# Revit family: L-Angle-Column
name_source: partatom
category: Structural Columns
revit_build: Autodesk Revit Architecture 2012 (Build: 20110210_1515)
units: mm (PartAtom-declared; Revit-internal decimal feet)

## types (127) — shared parameters
Assembly Code = B10

## per-type parameters (varying)
| type | A | W | b | d | k | t | x | y |
| L8X8X1-1/8 | 16.7 in² | 56.9 | 0' - 8" | 0' - 8" | 0' - 1 3/4" | 0' - 1 1/8" | 0' - 2 3/8" | 0' - 2 3/8" |
| L8X8X1 | 15 in² | 51 | 0' - 8" | 0' - 8" | 0' - 1 5/8" | 0' - 1" | 0' - 2 3/8" | 0' - 2 3/8" |
| L8X8X7/8 | 13.2 in² | 45 | 0' - 8" | 0' - 8" | 0' - 1 1/2" | 0' - 0 7/8" | 0' - 2 5/16" | 0' - 2 5/16" |
| L8X8X3/4 | 11.4 in² | 38.9 | 0' - 8" | 0' - 8" | 0' - 1 3/8" | 0' - 0 3/4" | 0' - 2 1/4" | 0' - 2 1/4" |
| L8X8X5/8 | 9.61 in² | 32.7 | 0' - 8" | 0' - 8" | 0' - 1 1/4" | 0' - 0 5/8" | 0' - 2 3/16" | 0' - 2 3/16" |
| L8X8X9/16 | 8.68 in² | 29.6 | 0' - 8" | 0' - 8" | 0' - 1 3/16" | 0' - 0 9/16" | 0' - 2 3/16" | 0' - 2 3/16" |
| L8X8X1/2 | 7.75 in² | 26.4 | 0' - 8" | 0' - 8" | 0' - 1 1/8" | 0' - 0 1/2" | 0' - 2 3/16" | 0' - 2 3/16" |
| L8X6X1 | 13 in² | 44.2 | 0' - 6" | 0' - 8" | 0' - 1 1/2" | 0' - 1" | 0' - 1 5/8" | 0' - 2 5/8" |
| L8X6X7/8 | 11.5 in² | 39.1 | 0' - 6" | 0' - 8" | 0' - 1 3/8" | 0' - 0 7/8" | 0' - 1 5/8" | 0' - 2 5/8" |
| L8X6X3/4 | 9.94 in² | 33.8 | 0' - 6" | 0' - 8" | 0' - 1 1/4" | 0' - 0 3/4" | 0' - 1 9/16" | 0' - 2 9/16" |
| L8X6X5/8 | 8.36 in² | 28.5 | 0' - 6" | 0' - 8" | 0' - 1 1/8" | 0' - 0 5/8" | 0' - 1 1/2" | 0' - 2 1/2" |
| L8X6X9/16 | 7.56 in² | 25.7 | 0' - 6" | 0' - 8" | 0' - 1 1/16" | 0' - 0 9/16" | 0' - 1 1/2" | 0' - 2 1/2" |
| L8X6X1/2 | 6.75 in² | 23 | 0' - 6" | 0' - 8" | 0' - 1" | 0' - 0 1/2" | 0' - 1 7/16" | 0' - 2 7/16" |
| L8X6X7/16 | 5.93 in² | 20.2 | 0' - 6" | 0' - 8" | 0' - 0 15/16" | 0' - 0 7/16" | 0' - 1 7/16" | 0' - 2 7/16" |
| L8X4X1 | 11 in² | 37.4 | 0' - 4" | 0' - 8" | 0' - 1 1/2" | 0' - 1" | 0' - 1 1/16" | 0' - 3" |
| L8X4X7/8 | 9.73 in² | 33.1 | 0' - 4" | 0' - 8" | 0' - 1 3/8" | 0' - 0 7/8" | 0' - 1" | 0' - 3" |
| L8X4X3/4 | 8.44 in² | 28.7 | 0' - 4" | 0' - 8" | 0' - 1 1/4" | 0' - 0 3/4" | 0' - 0 15/16" | 0' - 2 15/16" |
| L8X4X5/8 | 7.11 in² | 24.2 | 0' - 4" | 0' - 8" | 0' - 1 1/8" | 0' - 0 5/8" | 0' - 0 7/8" | 0' - 2 7/8" |
| L8X4X9/16 | 6.43 in² | 21.9 | 0' - 4" | 0' - 8" | 0' - 1 1/16" | 0' - 0 9/16" | 0' - 0 7/8" | 0' - 2 7/8" |
| L8X4X1/2 | 5.75 in² | 19.6 | 0' - 4" | 0' - 8" | 0' - 1" | 0' - 0 1/2" | 0' - 0 7/8" | 0' - 2 13/16" |
| L8X4X7/16 | 5.06 in² | 17.2 | 0' - 4" | 0' - 8" | 0' - 0 15/16" | 0' - 0 7/16" | 0' - 0 13/16" | 0' - 2 13/16" |
| L7X4X3/4 | 7.69 in² | 26.2 | 0' - 4" | 0' - 7" | 0' - 1 1/4" | 0' - 0 3/4" | 0' - 1" | 0' - 2 1/2" |
| L7X4X5/8 | 6.48 in² | 22.1 | 0' - 4" | 0' - 7" | 0' - 1 1/8" | 0' - 0 5/8" | 0' - 0 15/16" | 0' - 2 7/16" |
| L7X4X1/2 | 5.25 in² | 17.9 | 0' - 4" | 0' - 7" | 0' - 1" | 0' - 0 1/2" | 0' - 0 15/16" | 0' - 2 3/8" |
| L7X4X7/16 | 4.62 in² | 15.7 | 0' - 4" | 0' - 7" | 0' - 0 15/16" | 0' - 0 7/16" | 0' - 0 7/8" | 0' - 2 3/8" |
| L7X4X3/8 | 3.98 in² | 13.6 | 0' - 4" | 0' - 7" | 0' - 0 7/8" | 0' - 0 3/8" | 0' - 0 7/8" | 0' - 2 3/8" |
| L6X6X1 | 11 in² | 37.4 | 0' - 6" | 0' - 6" | 0' - 1 1/2" | 0' - 1" | 0' - 1 7/8" | 0' - 1 7/8" |
| L6X6X7/8 | 9.75 in² | 33.1 | 0' - 6" | 0' - 6" | 0' - 1 3/8" | 0' - 0 7/8" | 0' - 1 13/16" | 0' - 1 13/16" |
| L6X6X3/4 | 8.46 in² | 28.7 | 0' - 6" | 0' - 6" | 0' - 1 1/4" | 0' - 0 3/4" | 0' - 1 3/4" | 0' - 1 3/4" |
| L6X6X5/8 | 7.13 in² | 24.2 | 0' - 6" | 0' - 6" | 0' - 1 1/8" | 0' - 0 5/8" | 0' - 1 3/4" | 0' - 1 3/4" |
| L6X6X9/16 | 6.45 in² | 21.9 | 0' - 6" | 0' - 6" | 0' - 1 1/16" | 0' - 0 9/16" | 0' - 1 11/16" | 0' - 1 11/16" |
| L6X6X1/2 | 5.77 in² | 19.6 | 0' - 6" | 0' - 6" | 0' - 1" | 0' - 0 1/2" | 0' - 1 11/16" | 0' - 1 11/16" |
| L6X6X7/16 | 5.08 in² | 17.2 | 0' - 6" | 0' - 6" | 0' - 0 15/16" | 0' - 0 7/16" | 0' - 1 5/8" | 0' - 1 5/8" |
| L6X6X3/8 | 4.38 in² | 14.9 | 0' - 6" | 0' - 6" | 0' - 0 7/8" | 0' - 0 3/8" | 0' - 1 5/8" | 0' - 1 5/8" |
| L6X6X5/16 | 3.67 in² | 12.4 | 0' - 6" | 0' - 6" | 0' - 0 13/16" | 0' - 0 5/16" | 0' - 1 5/8" | 0' - 1 5/8" |
| L6X4X7/8 | 7.98 in² | 27.2 | 0' - 4" | 0' - 6" | 0' - 1 3/8" | 0' - 0 7/8" | 0' - 1 1/8" | 0' - 2 1/8" |
| L6X4X3/4 | 6.94 in² | 23.6 | 0' - 4" | 0' - 6" | 0' - 1 1/4" | 0' - 0 3/4" | 0' - 1 1/16" | 0' - 2 1/16" |
| L6X4X5/8 | 5.86 in² | 20 | 0' - 4" | 0' - 6" | 0' - 1 1/8" | 0' - 0 5/8" | 0' - 1" | 0' - 2" |
| L6X4X9/16 | 5.31 in² | 18.1 | 0' - 4" | 0' - 6" | 0' - 1 1/16" | 0' - 0 9/16" | 0' - 1" | 0' - 2" |
| L6X4X1/2 | 4.75 in² | 16.2 | 0' - 4" | 0' - 6" | 0' - 1" | 0' - 0 1/2" | 0' - 1" | 0' - 2" |
| L6X4X7/16 | 4.18 in² | 14.3 | 0' - 4" | 0' - 6" | 0' - 0 15/16" | 0' - 0 7/16" | 0' - 0 15/16" | 0' - 1 15/16" |
| L6X4X3/8 | 3.61 in² | 12.3 | 0' - 4" | 0' - 6" | 0' - 0 7/8" | 0' - 0 3/8" | 0' - 0 15/16" | 0' - 1 15/16" |
| L6X4X5/16 | 3.03 in² | 10.3 | 0' - 4" | 0' - 6" | 0' - 0 13/16" | 0' - 0 5/16" | 0' - 0 15/16" | 0' - 1 7/8" |
| L6X3-1/2X1/2 | 4.5 in² | 15.3 | 0' - 3 1/2" | 0' - 6" | 0' - 1" | 0' - 0 1/2" | 0' - 0 13/16" | 0' - 2 1/16" |
| L6X3-1/2X3/8 | 3.42 in² | 11.7 | 0' - 3 1/2" | 0' - 6" | 0' - 0 7/8" | 0' - 0 3/8" | 0' - 0 3/4" | 0' - 2" |
| L6X3-1/2X5/16 | 2.87 in² | 9.8 | 0' - 3 1/2" | 0' - 6" | 0' - 0 13/16" | 0' - 0 5/16" | 0' - 0 3/4" | 0' - 2" |
| L5X5X7/8 | 7.98 in² | 27.2 | 0' - 5" | 0' - 5" | 0' - 1 3/8" | 0' - 0 7/8" | 0' - 1 9/16" | 0' - 1 9/16" |
| L5X5X3/4 | 6.94 in² | 23.6 | 0' - 5" | 0' - 5" | 0' - 1 1/4" | 0' - 0 3/4" | 0' - 1 1/2" | 0' - 1 1/2" |
| L5X5X5/8 | 5.86 in² | 20 | 0' - 5" | 0' - 5" | 0' - 1 1/8" | 0' - 0 5/8" | 0' - 1 1/2" | 0' - 1 1/2" |
| L5X5X1/2 | 4.75 in² | 16.2 | 0' - 5" | 0' - 5" | 0' - 1" | 0' - 0 1/2" | 0' - 1 7/16" | 0' - 1 7/16" |
| L5X5X7/16 | 4.18 in² | 14.3 | 0' - 5" | 0' - 5" | 0' - 0 15/16" | 0' - 0 7/16" | 0' - 1 3/8" | 0' - 1 3/8" |
| L5X5X3/8 | 3.61 in² | 12.3 | 0' - 5" | 0' - 5" | 0' - 0 7/8" | 0' - 0 3/8" | 0' - 1 3/8" | 0' - 1 3/8" |
| L5X5X5/16 | 3.03 in² | 10.3 | 0' - 5" | 0' - 5" | 0' - 0 13/16" | 0' - 0 5/16" | 0' - 1 3/8" | 0' - 1 3/8" |
| L5X3-1/2X3/4 | 5.81 in² | 19.8 | 0' - 3 1/2" | 0' - 5" | 0' - 1 3/16" | 0' - 0 3/4" | 0' - 1" | 0' - 1 3/4" |
| L5X3-1/2X5/8 | 4.92 in² | 16.8 | 0' - 3 1/2" | 0' - 5" | 0' - 1 1/16" | 0' - 0 5/8" | 0' - 0 15/16" | 0' - 1 11/16" |
| L5X3-1/2X1/2 | 4 in² | 13.6 | 0' - 3 1/2" | 0' - 5" | 0' - 0 15/16" | 0' - 0 1/2" | 0' - 0 7/8" | 0' - 1 5/8" |
| L5X3-1/2X3/8 | 3.05 in² | 10.4 | 0' - 3 1/2" | 0' - 5" | 0' - 0 13/16" | 0' - 0 3/8" | 0' - 0 7/8" | 0' - 1 5/8" |
| L5X3-1/2X5/16 | 2.56 in² | 8.7 | 0' - 3 1/2" | 0' - 5" | 0' - 0 3/4" | 0' - 0 5/16" | 0' - 0 13/16" | 0' - 1 9/16" |
| L5X3-1/2X1/4 | 2.06 in² | 7 | 0' - 3 1/2" | 0' - 5" | 0' - 0 11/16" | 0' - 0 1/4" | 0' - 0 13/16" | 0' - 1 9/16" |
| L5X3X1/2 | 3.75 in² | 12.8 | 0' - 3" | 0' - 5" | 0' - 0 15/16" | 0' - 0 1/2" | 0' - 0 3/4" | 0' - 1 3/4" |
| L5X3X7/16 | 3.31 in² | 11.3 | 0' - 3" | 0' - 5" | 0' - 0 7/8" | 0' - 0 7/16" | 0' - 0 3/4" | 0' - 1 3/4" |
| L5X3X3/8 | 2.86 in² | 9.8 | 0' - 3" | 0' - 5" | 0' - 0 13/16" | 0' - 0 3/8" | 0' - 0 11/16" | 0' - 1 11/16" |
| L5X3X5/16 | 2.4 in² | 8.2 | 0' - 3" | 0' - 5" | 0' - 0 3/4" | 0' - 0 5/16" | 0' - 0 11/16" | 0' - 1 11/16" |
| L5X3X1/4 | 1.94 in² | 6.6 | 0' - 3" | 0' - 5" | 0' - 0 11/16" | 0' - 0 1/4" | 0' - 0 5/8" | 0' - 1 5/8" |
| L4X4X3/4 | 5.44 in² | 18.5 | 0' - 4" | 0' - 4" | 0' - 1 1/8" | 0' - 0 3/4" | 0' - 1 1/4" | 0' - 1 1/4" |
| L4X4X5/8 | 4.61 in² | 15.7 | 0' - 4" | 0' - 4" | 0' - 1" | 0' - 0 5/8" | 0' - 1 1/4" | 0' - 1 1/4" |
| L4X4X1/2 | 3.75 in² | 12.8 | 0' - 4" | 0' - 4" | 0' - 0 7/8" | 0' - 0 1/2" | 0' - 1 3/16" | 0' - 1 3/16" |
| L4X4X7/16 | 3.31 in² | 11.3 | 0' - 4" | 0' - 4" | 0' - 0 13/16" | 0' - 0 7/16" | 0' - 1 1/8" | 0' - 1 1/8" |
| L4X4X3/8 | 2.86 in² | 9.8 | 0' - 4" | 0' - 4" | 0' - 0 3/4" | 0' - 0 3/8" | 0' - 1 1/8" | 0' - 1 1/8" |
| L4X4X5/16 | 2.4 in² | 8.2 | 0' - 4" | 0' - 4" | 0' - 0 11/16" | 0' - 0 5/16" | 0' - 1 1/8" | 0' - 1 1/8" |
| L4X4X1/4 | 1.94 in² | 6.6 | 0' - 4" | 0' - 4" | 0' - 0 5/8" | 0' - 0 1/4" | 0' - 1 1/16" | 0' - 1 1/16" |
| L4X3-1/2X1/2 | 3.5 in² | 11.9 | 0' - 3 1/2" | 0' - 4" | 0' - 0 7/8" | 0' - 0 1/2" | 0' - 1" | 0' - 1 1/4" |
| L4X3-1/2X3/8 | 2.67 in² | 9.1 | 0' - 3 1/2" | 0' - 4" | 0' - 0 3/4" | 0' - 0 3/8" | 0' - 0 15/16" | 0' - 1 3/16" |
| L4X3-1/2X5/16 | 2.25 in² | 7.7 | 0' - 3 1/2" | 0' - 4" | 0' - 0 11/16" | 0' - 0 5/16" | 0' - 0 15/16" | 0' - 1 3/16" |
| L4X3-1/2X1/4 | 1.81 in² | 6.2 | 0' - 3 1/2" | 0' - 4" | 0' - 0 5/8" | 0' - 0 1/4" | 0' - 0 7/8" | 0' - 1 1/8" |
| L4X3X5/8 | 3.89 in² | 13.6 | 0' - 3" | 0' - 4" | 0' - 1" | 0' - 0 5/8" | 0' - 0 7/8" | 0' - 1 3/8" |
| L4X3X1/2 | 3.25 in² | 11.1 | 0' - 3" | 0' - 4" | 0' - 0 7/8" | 0' - 0 1/2" | 0' - 0 13/16" | 0' - 1 5/16" |
| L4X3X3/8 | 2.48 in² | 8.5 | 0' - 3" | 0' - 4" | 0' - 0 3/4" | 0' - 0 3/8" | 0' - 0 3/4" | 0' - 1 1/4" |
| L4X3X5/16 | 2.09 in² | 7.2 | 0' - 3" | 0' - 4" | 0' - 0 11/16" | 0' - 0 5/16" | 0' - 0 3/4" | 0' - 1 1/4" |
| L4X3X1/4 | 1.69 in² | 5.8 | 0' - 3" | 0' - 4" | 0' - 0 5/8" | 0' - 0 1/4" | 0' - 0 3/4" | 0' - 1 1/4" |
| L3-1/2X3-1/2X1/2 | 3.25 in² | 11.1 | 0' - 3 1/2" | 0' - 3 1/2" | 0' - 0 7/8" | 0' - 0 1/2" | 0' - 1 1/16" | 0' - 1 1/16" |
| L3-1/2X3-1/2X7/16 | 2.87 in² | 9.8 | 0' - 3 1/2" | 0' - 3 1/2" | 0' - 0 13/16" | 0' - 0 7/16" | 0' - 1" | 0' - 1" |
| L3-1/2X3-1/2X3/8 | 2.48 in² | 8.5 | 0' - 3 1/2" | 0' - 3 1/2" | 0' - 0 3/4" | 0' - 0 3/8" | 0' - 1" | 0' - 1" |
| L3-1/2X3-1/2X5/16 | 2.09 in² | 7.2 | 0' - 3 1/2" | 0' - 3 1/2" | 0' - 0 11/16" | 0' - 0 5/16" | 0' - 1" | 0' - 1" |
| L3-1/2X3-1/2X1/4 | 1.69 in² | 5.8 | 0' - 3 1/2" | 0' - 3 1/2" | 0' - 0 5/8" | 0' - 0 1/4" | 0' - 0 15/16" | 0' - 0 15/16" |
| L3-1/2X3X1/2 | 3 in² | 10.2 | 0' - 3" | 0' - 3 1/2" | 0' - 0 7/8" | 0' - 0 1/2" | 0' - 0 7/8" | 0' - 1 1/8" |
| L3-1/2X3X7/16 | 2.65 in² | 9.1 | 0' - 3" | 0' - 3 1/2" | 0' - 0 13/16" | 0' - 0 7/16" | 0' - 0 7/8" | 0' - 1 1/16" |
| L3-1/2X3X3/8 | 2.3 in² | 7.9 | 0' - 3" | 0' - 3 1/2" | 0' - 0 3/4" | 0' - 0 3/8" | 0' - 0 13/16" | 0' - 1 1/16" |
| L3-1/2X3X5/16 | 1.93 in² | 6.6 | 0' - 3" | 0' - 3 1/2" | 0' - 0 11/16" | 0' - 0 5/16" | 0' - 0 13/16" | 0' - 1 1/16" |
| L3-1/2X3X1/4 | 1.56 in² | 5.4 | 0' - 3" | 0' - 3 1/2" | 0' - 0 5/8" | 0' - 0 1/4" | 0' - 0 3/4" | 0' - 1" |
| L3-1/2X2-1/2X1/2 | 2.75 in² | 9.4 | 0' - 2 1/2" | 0' - 3 1/2" | 0' - 0 7/8" | 0' - 0 1/2" | 0' - 0 11/16" | 0' - 1 3/16" |
| L3-1/2X2-1/2X3/8 | 2.11 in² | 7.2 | 0' - 2 1/2" | 0' - 3 1/2" | 0' - 0 3/4" | 0' - 0 3/8" | 0' - 0 5/8" | 0' - 1 1/8" |
| L3-1/2X2-1/2X5/16 | 1.78 in² | 6.1 | 0' - 2 1/2" | 0' - 3 1/2" | 0' - 0 11/16" | 0' - 0 5/16" | 0' - 0 5/8" | 0' - 1 1/8" |
| L3-1/2X2-1/2X1/4 | 1.44 in² | 4.9 | 0' - 2 1/2" | 0' - 3 1/2" | 0' - 0 5/8" | 0' - 0 1/4" | 0' - 0 5/8" | 0' - 1 1/8" |
| L3X3X1/2 | 2.75 in² | 9.4 | 0' - 3" | 0' - 3" | 0' - 0 7/8" | 0' - 0 1/2" | 0' - 0 15/16" | 0' - 0 15/16" |
| L3X3X7/16 | 2.43 in² | 8.3 | 0' - 3" | 0' - 3" | 0' - 0 13/16" | 0' - 0 7/16" | 0' - 0 15/16" | 0' - 0 15/16" |
| L3X3X3/8 | 2.11 in² | 7.2 | 0' - 3" | 0' - 3" | 0' - 0 3/4" | 0' - 0 3/8" | 0' - 0 7/8" | 0' - 0 7/8" |
| L3X3X5/16 | 1.78 in² | 6.1 | 0' - 3" | 0' - 3" | 0' - 0 11/16" | 0' - 0 5/16" | 0' - 0 7/8" | 0' - 0 7/8" |
| L3X3X1/4 | 1.44 in² | 4.9 | 0' - 3" | 0' - 3" | 0' - 0 5/8" | 0' - 0 1/4" | 0' - 0 13/16" | 0' - 0 13/16" |
| L3X3X3/16 | 1.09 in² | 3.71 | 0' - 3" | 0' - 3" | 0' - 0 9/16" | 0' - 0 3/16" | 0' - 0 13/16" | 0' - 0 13/16" |
| L3X2-1/2X1/2 | 2.5 in² | 8.5 | 0' - 2 1/2" | 0' - 3" | 0' - 0 7/8" | 0' - 0 1/2" | 0' - 0 3/4" | 0' - 1" |
| L3X2-1/2X7/16 | 2.21 in² | 7.6 | 0' - 2 1/2" | 0' - 3" | 0' - 0 13/16" | 0' - 0 7/16" | 0' - 0 3/4" | 0' - 1" |
| L3X2-1/2X3/8 | 1.92 in² | 6.6 | 0' - 2 1/2" | 0' - 3" | 0' - 0 3/4" | 0' - 0 3/8" | 0' - 0 11/16" | 0' - 0 15/16" |
| L3X2-1/2X5/16 | 1.67 in² | 5.6 | 0' - 2 1/2" | 0' - 3" | 0' - 0 11/16" | 0' - 0 5/16" | 0' - 0 11/16" | 0' - 0 15/16" |
| L3X2-1/2X1/4 | 1.31 in² | 4.5 | 0' - 2 1/2" | 0' - 3" | 0' - 0 5/8" | 0' - 0 1/4" | 0' - 0 5/8" | 0' - 0 7/8" |
| L3X2-1/2X3/16 | 1 in² | 3.39 | 0' - 2 1/2" | 0' - 3" | 0' - 0 9/16" | 0' - 0 3/16" | 0' - 0 5/8" | 0' - 0 7/8" |
| L3X2X1/2 | 2.25 in² | 7.7 | 0' - 2" | 0' - 3" | 0' - 0 13/16" | 0' - 0 1/2" | 0' - 0 9/16" | 0' - 1 1/16" |
| L3X2X3/8 | 1.73 in² | 5.9 | 0' - 2" | 0' - 3" | 0' - 0 11/16" | 0' - 0 3/8" | 0' - 0 9/16" | 0' - 1" |
| L3X2X5/16 | 1.46 in² | 5 | 0' - 2" | 0' - 3" | 0' - 0 5/8" | 0' - 0 5/16" | 0' - 0 1/2" | 0' - 1" |
| L3X2X1/4 | 1.19 in² | 4.1 | 0' - 2" | 0' - 3" | 0' - 0 9/16" | 0' - 0 1/4" | 0' - 0 1/2" | 0' - 1" |
| L3X2X3/16 | 0.9 in² | 3.07 | 0' - 2" | 0' - 3" | 0' - 0 1/2" | 0' - 0 3/16" | 0' - 0 7/16" | 0' - 0 15/16" |
| L2-1/2X2-1/2X1/2 | 2.25 in² | 7.7 | 0' - 2 1/2" | 0' - 2 1/2" | 0' - 0 3/4" | 0' - 0 1/2" | 0' - 0 13/16" | 0' - 0 13/16" |
| L2-1/2X2-1/2X3/8 | 1.73 in² | 5.9 | 0' - 2 1/2" | 0' - 2 1/2" | 0' - 0 5/8" | 0' - 0 3/8" | 0' - 0 3/4" | 0' - 0 3/4" |
| L2-1/2X2-1/2X5/16 | 1.46 in² | 5 | 0' - 2 1/2" | 0' - 2 1/2" | 0' - 0 9/16" | 0' - 0 5/16" | 0' - 0 3/4" | 0' - 0 3/4" |
| L2-1/2X2-1/2X1/4 | 1.19 in² | 4.1 | 0' - 2 1/2" | 0' - 2 1/2" | 0' - 0 1/2" | 0' - 0 1/4" | 0' - 0 11/16" | 0' - 0 11/16" |
| L2-1/2X2-1/2X3/16 | 0.9 in² | 3.07 | 0' - 2 1/2" | 0' - 2 1/2" | 0' - 0 7/16" | 0' - 0 3/16" | 0' - 0 11/16" | 0' - 0 11/16" |
| L2-1/2X2X3/8 | 1.55 in² | 5.3 | 0' - 2" | 0' - 2 1/2" | 0' - 0 5/8" | 0' - 0 3/8" | 0' - 0 9/16" | 0' - 0 13/16" |
| L2-1/2X2X5/16 | 1.31 in² | 4.5 | 0' - 2" | 0' - 2 1/2" | 0' - 0 9/16" | 0' - 0 5/16" | 0' - 0 9/16" | 0' - 0 13/16" |
| L2-1/2X2X1/4 | 1.06 in² | 3.62 | 0' - 2" | 0' - 2 1/2" | 0' - 0 1/2" | 0' - 0 1/4" | 0' - 0 9/16" | 0' - 0 3/4" |
| L2-1/2X2X3/16 | 0.81 in² | 2.75 | 0' - 2" | 0' - 2 1/2" | 0' - 0 7/16" | 0' - 0 3/16" | 0' - 0 1/2" | 0' - 0 3/4" |
| L2-1/2X1-1/2X1/4 | 0.94 in² | 3.22 | 0' - 1 1/2" | 0' - 2 1/2" | 0' - 0 1/2" | 0' - 0 1/4" | 0' - 0 3/8" | 0' - 0 7/8" |
| L2-1/2X1-1/2X3/16 | 0.72 in² | 2.47 | 0' - 1 1/2" | 0' - 2 1/2" | 0' - 0 7/16" | 0' - 0 3/16" | 0' - 0 3/8" | 0' - 0 13/16" |
| L2X2X3/8 | 1.36 in² | 4.7 | 0' - 2" | 0' - 2" | 0' - 0 5/8" | 0' - 0 3/8" | 0' - 0 5/8" | 0' - 0 5/8" |
| L2X2X5/16 | 1.15 in² | 3.92 | 0' - 2" | 0' - 2" | 0' - 0 9/16" | 0' - 0 5/16" | 0' - 0 5/8" | 0' - 0 5/8" |
| L2X2X1/4 | 0.94 in² | 3.19 | 0' - 2" | 0' - 2" | 0' - 0 1/2" | 0' - 0 1/4" | 0' - 0 9/16" | 0' - 0 9/16" |
| L2X2X3/16 | 0.72 in² | 2.44 | 0' - 2" | 0' - 2" | 0' - 0 7/16" | 0' - 0 3/16" | 0' - 0 9/16" | 0' - 0 9/16" |
| L2X2X1/8 | 0.48 in² | 1.65 | 0' - 2" | 0' - 2" | 0' - 0 3/8" | 0' - 0 1/8" | 0' - 0 9/16" | 0' - 0 9/16" |

## geometry (parser evidence)
native form markers: Sweep x1
no freeform markers — native parametric forms only
